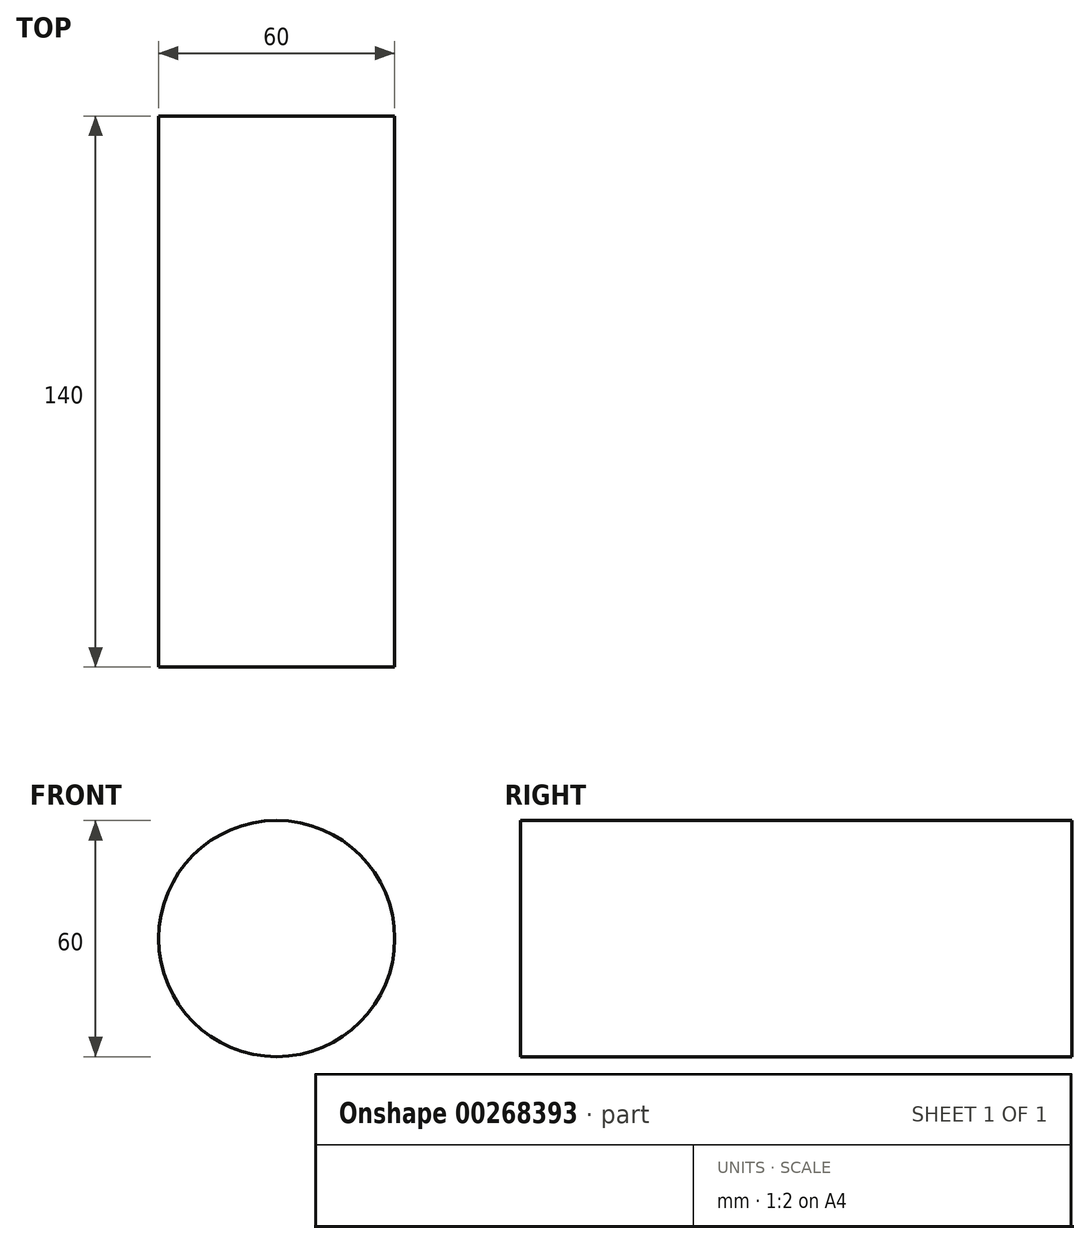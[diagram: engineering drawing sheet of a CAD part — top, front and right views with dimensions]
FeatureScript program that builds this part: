
annotation { "Feature Type Name" : "Feature", "Feature Type Description" : "" }
export const myFeature = defineFeature(function(context is Context, id is Id, definition is map)
    precondition{}
    {
        {
            var Q0;
            Q0=qCreatedBy(makeId("Front.planeOp"),FACE);
            var sketch = newSketch(context, id + "F0", { "sketchPlane" : qUnion([Q0])});
            skCircle(sketch, "E0", {"center": v(0, 0) * mm, "radius": 30 * mm});
            skSolve(sketch);
        }
        {
            var Q0;
            Q0 = qSketchRegion(id + "F0", true);
            extrude(context, id + "F1", {"entities" : qUnion([Q0]), "depth" : 140 * mm, "offsetDistance" : 25 * mm});
        }
    });
